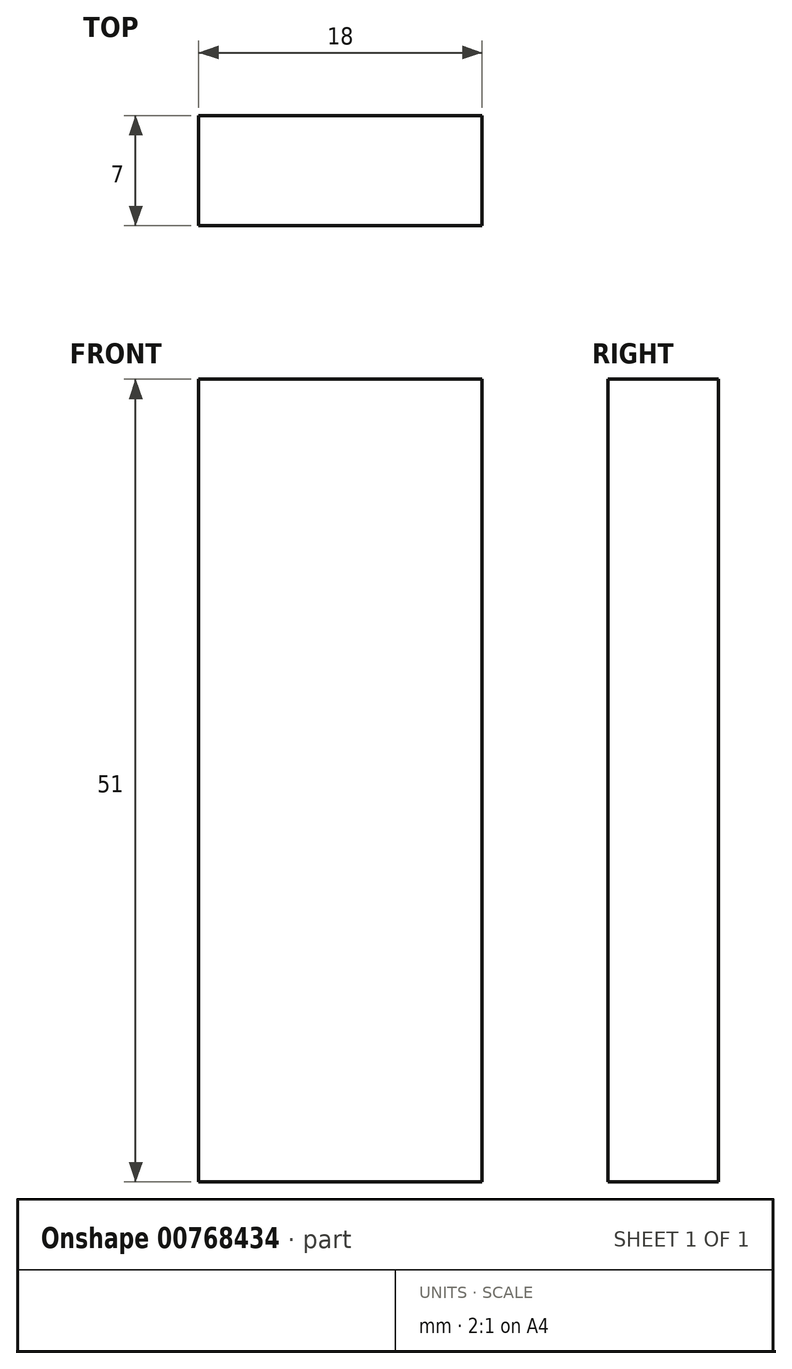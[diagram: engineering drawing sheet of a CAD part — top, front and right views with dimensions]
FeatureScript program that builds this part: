
annotation { "Feature Type Name" : "Feature", "Feature Type Description" : "" }
export const myFeature = defineFeature(function(context is Context, id is Id, definition is map)
    precondition{}
    {
        {
            var Q0;
            Q0=qCreatedBy(makeId("Front.planeOp"),FACE);
            var sketch = newSketch(context, id + "F0", { "sketchPlane" : qUnion([Q0])});
            skLineSegment(sketch, "E0.bottom", {"start": v(9, 25.5) * mm, "end": v(-9, 25.5) * mm});
            skLineSegment(sketch, "E0.top", {"start": v(9, -25.5) * mm, "end": v(-9, -25.5) * mm});
            skLineSegment(sketch, "E0.left", {"start": v(9, 25.5) * mm, "end": v(9, -25.5) * mm});
            skLineSegment(sketch, "E0.right", {"start": v(-9, 25.5) * mm, "end": v(-9, -25.5) * mm});
            skPoint(sketch, "E0.middle", {"position": v(0, 0) * mm});
            skSolve(sketch);
        }
        {
            var Q0;
            Q0=qSketchRegion(id+"F0",true);
            extrude(context, id + "F1", {"entities" : qUnion([Q0]), "depth" : 7 * mm, "offsetDistance" : 25 * mm});
        }
    });
